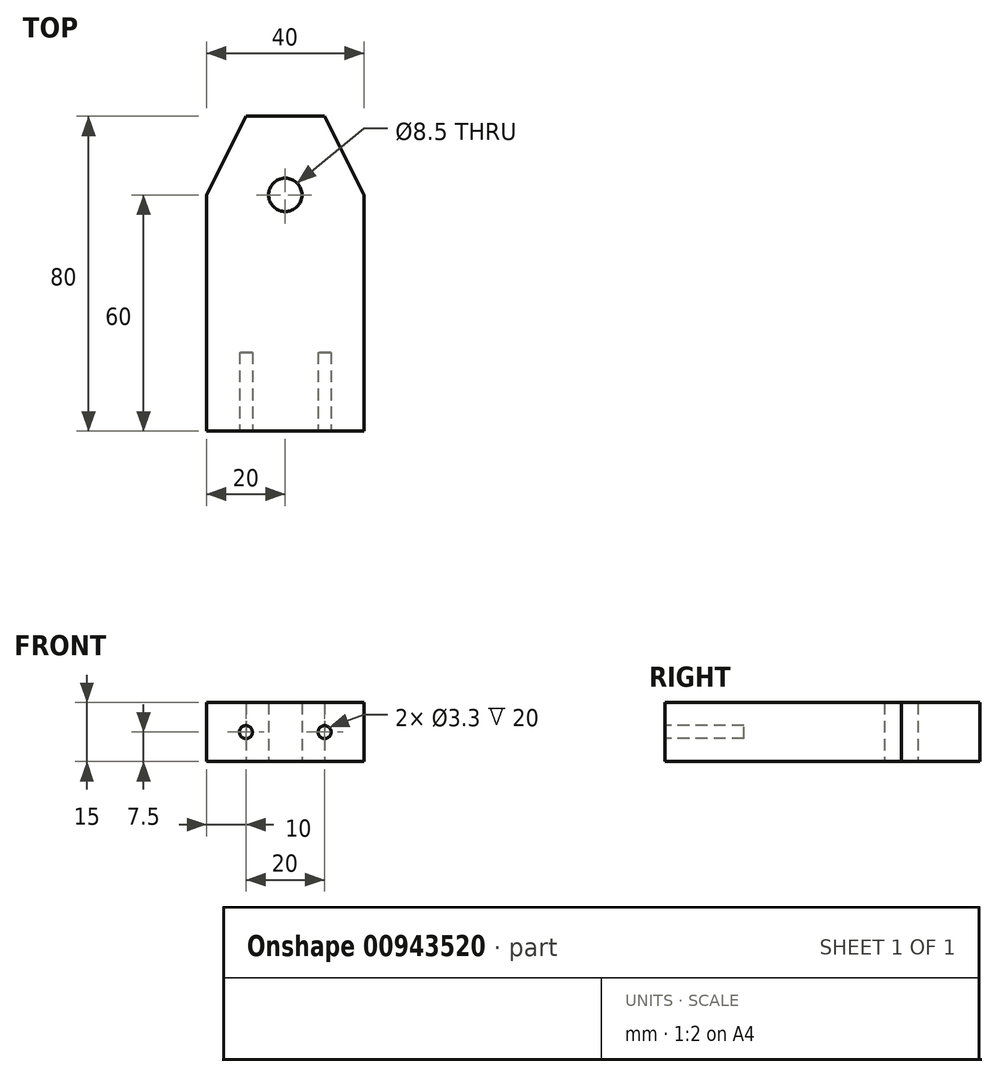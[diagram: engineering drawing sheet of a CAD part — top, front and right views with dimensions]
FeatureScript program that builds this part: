
annotation { "Feature Type Name" : "Feature", "Feature Type Description" : "" }
export const myFeature = defineFeature(function(context is Context, id is Id, definition is map)
    precondition{}
    {
        {
            var Q0;
            Q0=qCreatedBy(makeId("Top.planeOp"),FACE);
            var sketch = newSketch(context, id + "F0", { "sketchPlane" : qUnion([Q0])});
            skLineSegment(sketch, "E0", {"start": v(0, 0) * mm, "end": v(0, 20) * mm, "construction": true});
            skLineSegment(sketch, "E1", {"start": v(0, 20) * mm, "end": v(10, 20) * mm, "construction": true});
            skLineSegment(sketch, "E2", {"start": v(10, 20) * mm, "end": v(-10, 20) * mm, "construction": true});
            skLineSegment(sketch, "E3", {"start": v(0, 0) * mm, "end": v(0, -60) * mm, "construction": true});
            skLineSegment(sketch, "E4", {"start": v(0, -60) * mm, "end": v(20, -60) * mm, "construction": true});
            skLineSegment(sketch, "E5", {"start": v(20, -60) * mm, "end": v(-20, -60) * mm});
            skLineSegment(sketch, "E6", {"start": v(-10, 20) * mm, "end": v(10, 20) * mm});
            skCircle(sketch, "E7", {"center": v(0, 0) * mm, "radius": 4.25 * mm});
            skLineSegment(sketch, "E8", {"start": v(0, 0) * mm, "end": v(20, 0) * mm, "construction": true});
            skLineSegment(sketch, "E9", {"start": v(10, 20) * mm, "end": v(20, 0) * mm});
            skLineSegment(sketch, "E10", {"start": v(20, 0) * mm, "end": v(20, -60) * mm});
            skLineSegment(sketch, "E11", {"start": v(0, 0) * mm, "end": v(-20, 0) * mm, "construction": true});
            skLineSegment(sketch, "E12", {"start": v(-10, 20) * mm, "end": v(-20, 0) * mm});
            skLineSegment(sketch, "E13", {"start": v(-20, 0) * mm, "end": v(-20, -60) * mm});
            skSolve(sketch);
        }
        {
            var Q0;
            Q0=qSketchRegion(id+"F0",true);
            extrude(context, id + "F1", {"entities" : qUnion([Q0]), "depth" : 15 * mm, "offsetDistance" : 25 * mm});
        }
        {
            var Q0;
            Q0=makeQuery(id+"F1.opExtrude","SWEPT_FACE",FACE,{"disambiguationData":[OSD([sQuery(id+"F0.wireOp",EDGE,"E5")])]});
            var sketch = newSketch(context, id + "F2", { "sketchPlane" : qUnion([Q0])});
            skLineSegment(sketch, "E14", {"start": v(-20, 15) * mm, "end": v(-20, 7.5) * mm, "construction": true});
            skLineSegment(sketch, "E15", {"start": v(-20, 7.5) * mm, "end": v(-10, 7.5) * mm, "construction": true});
            skLineSegment(sketch, "E16", {"start": v(-10, 7.5) * mm, "end": v(10, 7.5) * mm, "construction": true});
            skCircle(sketch, "E17", {"center": v(10, 7.5) * mm, "radius": 1.65 * mm});
            skCircle(sketch, "E18", {"center": v(-10, 7.5) * mm, "radius": 1.65 * mm});
            skSolve(sketch);
        }
        {
            var Q0;
            Q0 = qSketchRegion(id + "F2", true);
            extrude(context, id + "F3", {"entities" : qUnion([Q0]), "operationType" : NewBodyOperationType.REMOVE, "oppositeDirection" : true, "depth" : 20 * mm, "offsetDistance" : 25 * mm});
        }
    });
